# Revit family: BE_77057_de_DE
name_source: partatom
category: Leuchten
revit_build: Autodesk Revit 2015 (Build: 20150704_0715(x64)
units: mm (PartAtom-declared; Revit-internal decimal feet)

## types (4) — shared parameters
AC/DC = AC/DC
Aktualisierung = 2016-03-16T04:08:46
Anschlussleitung = 1.8 m H07RN8-F 3 G 1,5²
BEGA_Dummy = Nein
BEGA_IES = Ja
BEGA_Intern = Ja
BEGA_Intern_Konstruktion = Ja
BEGA_Intern_an = Ja
BEGA_Intern_aus = Ja
Beschreibung = Bodeneinbauleuchte
Beschreibung_Sonderanfertigung = Hier können Sie Informationen zur Sonderanfertigung eintragen.
Bestellnummer_Einbaugehäuse = ---
CE_Konformität = ja
ENEC = ja
Einbau_in_Wärmedämmung = ungeeignet
Einbaugehäuse = Nein
Energieeffizienzklasse = LED A++ - A
Farbfilter = 16777215
Farbtemperaturverschiebung bei Dämpfen der Lampe = <Keine Auswahl>
Farbwiedergabeindex = Ra > 80
Frequenz = 0/50-60 Hz
Gewicht = 3.05 kg
Hersteller = BEGA
Lampe = LED 6.3 W
Lastklassifizierung = Beleuchtung
Lebensdauerkriterien = L70 = 50.000 h
Logo = BEGA_Logo.png
Material_06 = BEGA_Oberfläche_Edelstahl_gebürstet
Material_11 = BEGA_Glas_opal
Neigungswinkel = 0.00°
Oberflächentemperatur = 25 °C
Produktdatenblatt = http://www.bega.de
Scheinlast = 0 VA
Schutzart = IP 68...10m
Schutzklasse = I
Sonderanfertigung = Nein
Spannung = 0 V
Typenbild = 77057.png
URL = http://www.bega.de
zero-valued in all types: Vorgabe-Ansicht

## per-type parameters (varying)
| type | Bestellnummer | Datei für fotometrisches Netz | Farbtemperatur | LED_Modulbezeichnung | Lampenlichtstrom | Leuchtenlichtstrom | Modell | Rutschhemmendes_Glas |
| BEGA_77057_R_K3 | 77057RK3 | BE_77057K3.IES | 3000 K | LED-0271/830 | 735 lm | 155 lm | 77057RK3 | ja |
| BEGA_77057_K4 | 77057 | BE_77057.IES | 4000 K | LED-0271/840 | 790 lm | 167 lm | 77057 |  |
| BEGA_77057_K3 | 77057K3 | BE_77057K3.IES | 3000 K | LED-0271/830 | 735 lm | 155 lm | 77057K3 |  |
| BEGA_77057_R_K4 | 77057R | BE_77057.IES | 4000 K | LED-0271/840 | 790 lm | 167 lm | 77057R | ja |
